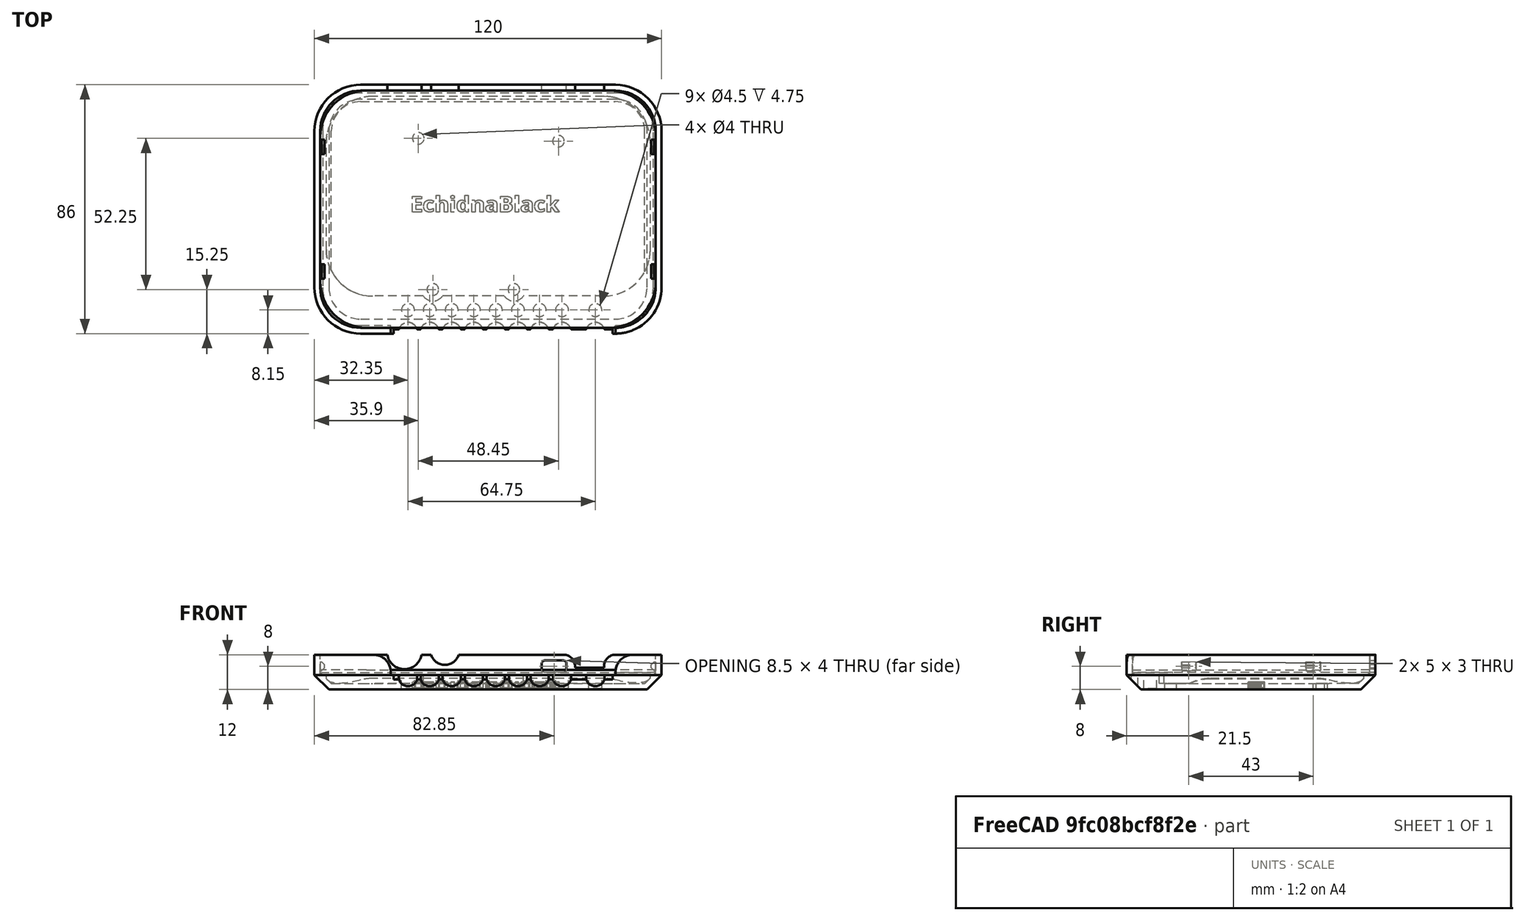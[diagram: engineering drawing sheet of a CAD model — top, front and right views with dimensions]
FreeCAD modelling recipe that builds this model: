
FCSTD DOCUMENT  (FreeCAD 0.18R4 (GitTag))
Label: Caixa_EchidaBlack_baja
License: All rights reserved
LicenseURL: http://en.wikipedia.org/wiki/All_rights_reserved
objects: Part::Cylinder×29, Part::Box×14, Part::Fillet×11, Part::Cut×11, Part::MultiFuse×8, Part::Chamfer×6, Part::Thickness×2, Part::Part2DObjectPython×1, Part::Extrusion×1, Mesh::Feature×1
note: 83 computed .brp shape members not serialized (recipe doc carries the construction recipe); baked Part::Feature solids carry a one-line shape summary decoded from their .brp

FEATURE [Part::Box] Box006  label="Cubo006"
  AttacherType = Attacher::AttachEngine3D
  Height = 9
  Length = 10
  Placement = pos=(83,76,0.5) rot=(0,0,1;0rad)
  Width = 8
FEATURE [Part::Box] Box013  label="Cubo013"
  AttacherType = Attacher::AttachEngine3D
  Height = 12
  Length = 77.75
  Placement = pos=(19.25,-4,-2) rot=(0,0,1;0rad)
  Width = 10
FEATURE [Part::Cylinder] Cylinder005  label="Cilindro005"
  Angle = 360
  AttacherType = Attacher::AttachEngine3D
  Height = 12
  Placement = pos=(32.75,5.15,-9) rot=(0,0,1;0rad)
  Radius = 2.25
FEATURE [Part::Cylinder] Cylinder006  label="Cilindro006"
  Angle = 360
  AttacherType = Attacher::AttachEngine3D
  Height = 12
  Placement = pos=(25.25,5.15,-9) rot=(0,0,1;0rad)
  Radius = 2.25
FEATURE [Part::Cylinder] Cylinder007  label="Cilindro007"
  Angle = 360
  AttacherType = Attacher::AttachEngine3D
  Height = 12
  Placement = pos=(40.35,5.15,-9) rot=(0,0,1;0rad)
  Radius = 2.25
FEATURE [Part::Cylinder] Cylinder008  label="Cilindro008"
  Angle = 360
  AttacherType = Attacher::AttachEngine3D
  Height = 12
  Placement = pos=(48,5.15,-9) rot=(0,0,1;0rad)
  Radius = 2.25
FEATURE [Part::Cylinder] Cylinder009  label="Cilindro009"
  Angle = 360
  AttacherType = Attacher::AttachEngine3D
  Height = 12
  Placement = pos=(55.6,5.15,-9) rot=(0,0,1;0rad)
  Radius = 2.25
FEATURE [Part::Cylinder] Cylinder010  label="Cilindro010"
  Angle = 360
  AttacherType = Attacher::AttachEngine3D
  Height = 12
  Placement = pos=(63.25,5.15,-9) rot=(0,0,1;0rad)
  Radius = 2.25
FEATURE [Part::Cylinder] Cylinder011  label="Cilindro011"
  Angle = 360
  AttacherType = Attacher::AttachEngine3D
  Height = 12
  Placement = pos=(70.75,5.15,-9) rot=(0,0,1;0rad)
  Radius = 2.25
FEATURE [Part::Cylinder] Cylinder012  label="Cilindro012"
  Angle = 360
  AttacherType = Attacher::AttachEngine3D
  Height = 12
  Placement = pos=(70.75,5.15,-9) rot=(0,0,1;0rad)
  Radius = 2.25
FEATURE [Part::Cylinder] Cylinder013  label="Cilindro013"
  Angle = 360
  AttacherType = Attacher::AttachEngine3D
  Height = 12
  Placement = pos=(78.5,5.15,-9) rot=(0,0,1;0rad)
  Radius = 2.25
FEATURE [Part::Cylinder] Cylinder014  label="Cilindro014"
  Angle = 360
  AttacherType = Attacher::AttachEngine3D
  Height = 12
  Placement = pos=(90,5.15,-9) rot=(0,0,1;0rad)
  Radius = 2.25
FEATURE [Part::MultiFuse] Fusion  label="FusionCilindros"
  Placement = pos=(0,0,2.25) rot=(0,0,1;0rad)
  Shapes = -> [Cylinder005,Cylinder006,Cylinder009,Cylinder013,Cylinder011,Cylinder012,Cylinder007,Cylinder008,Cylinder010,Cylinder014]
FEATURE [Part::Part2DObjectPython] ShapeString  # Draft 2D object (typed FeaturePython)
  FontFile = <path>
  MapMode = 5
  Placement = pos=(26,39,-11) rot=(0,0,1;0rad)
  Size = 7
  String = EchidnaBlack
  Tracking = 0
FEATURE [Part::Box] Box016  label="Cubo016"
  AttacherType = Attacher::AttachEngine3D
  Height = 4
  Length = 8.5
  Placement = pos=(72,75,-1) rot=(0,0,1;0rad)
  Width = 8
FEATURE [Part::Cylinder] Cylinder  label="Cilindro"
  Angle = 360
  AttacherType = Attacher::AttachEngine3D
  Height = 10
  Placement = pos=(38,88,6.5) rot=(1,0,0;1.5708rad)
  Radius = 5
FEATURE [Part::Cylinder] Cylinder025  label="Cilindro025"
  Angle = 360
  AttacherType = Attacher::AttachEngine3D
  Height = 10
  Placement = pos=(24,88,6) rot=(1,0,0;1.5708rad)
  Radius = 6
FEATURE [Part::Box] Box  label="Cubo"
  AttacherType = Attacher::AttachEngine3D
  Height = 3
  Length = 2
  Placement = pos=(-5.25,27,-2) rot=(0,0,1;0rad)
  Width = 5
FEATURE [Part::Box] Box017  label="Cubo017"
  AttacherType = Attacher::AttachEngine3D
  Height = 3
  Length = 2
  Placement = pos=(109,27,-2) rot=(0,0,1;0rad)
  Width = 5
FEATURE [Part::Chamfer] Chamfer001
  Base = -> Box017
  Edges = 2 edges r=1: [Edge2,Edge4]
  Placement = pos=(0.3,-11,1.5) rot=(0,0,1;0rad)
FEATURE [Part::Box] Box018  label="Cubo018"
  AttacherType = Attacher::AttachEngine3D
  Height = 3
  Length = 2
  Placement = pos=(-5.25,27,-2) rot=(0,0,1;0rad)
  Width = 5
FEATURE [Part::Chamfer] Chamfer002
  Base = -> Box018
  Edges = 2 edges r=1: [Edge6,Edge8]
  Placement = pos=(-0.3,32,1.5) rot=(0,0,1;0rad)
FEATURE [Part::Box] Box019  label="Cubo019"
  AttacherType = Attacher::AttachEngine3D
  Height = 3
  Length = 2
  Placement = pos=(109,27,-2) rot=(0,0,1;0rad)
  Width = 5
FEATURE [Part::Chamfer] Chamfer003
  Base = -> Box019
  Edges = 2 edges r=1: [Edge2,Edge4]
  Placement = pos=(0.3,32,1.5) rot=(0,0,1;0rad)
FEATURE [Part::Fillet] Fillet028
  Base = -> Box016
  Edges = 4 edges r=1: [Edge2,Edge4,Edge6,Edge8]
  Placement = pos=(-0.5,1,0) rot=(0,0,1;0rad)
FEATURE [Part::Cylinder] Cylinder036  label="Cilindro036"
  Angle = 360
  AttacherType = Attacher::AttachEngine3D
  Height = 12
  Placement = pos=(70.75,5.15,-9) rot=(0,0,1;0rad)
  Radius = 3.25
FEATURE [Part::Cylinder] Cylinder037  label="Cilindro037"
  Angle = 360
  AttacherType = Attacher::AttachEngine3D
  Height = 12
  Placement = pos=(70.75,5.15,-9) rot=(0,0,1;0rad)
  Radius = 3.25
FEATURE [Part::Cylinder] Cylinder038  label="Cilindro038"
  Angle = 360
  AttacherType = Attacher::AttachEngine3D
  Height = 12
  Placement = pos=(78.5,5.15,-9) rot=(0,0,1;0rad)
  Radius = 3.25
FEATURE [Part::Cylinder] Cylinder039  label="Cilindro039"
  Angle = 360
  AttacherType = Attacher::AttachEngine3D
  Height = 12
  Placement = pos=(90,5.15,-9) rot=(0,0,1;0rad)
  Radius = 3.25
FEATURE [Part::Cylinder] Cylinder040  label="Cilindro040"
  Angle = 360
  AttacherType = Attacher::AttachEngine3D
  Height = 12
  Placement = pos=(32.75,5.15,-9) rot=(0,0,1;0rad)
  Radius = 3.25
FEATURE [Part::Cylinder] Cylinder041  label="Cilindro041"
  Angle = 360
  AttacherType = Attacher::AttachEngine3D
  Height = 12
  Placement = pos=(25.25,5.15,-9) rot=(0,0,1;0rad)
  Radius = 3.25
FEATURE [Part::Cylinder] Cylinder042  label="Cilindro042"
  Angle = 360
  AttacherType = Attacher::AttachEngine3D
  Height = 12
  Placement = pos=(40.35,5.15,-9) rot=(0,0,1;0rad)
  Radius = 3.25
FEATURE [Part::Cylinder] Cylinder043  label="Cilindro043"
  Angle = 360
  AttacherType = Attacher::AttachEngine3D
  Height = 12
  Placement = pos=(48,5.15,-9) rot=(0,0,1;0rad)
  Radius = 3.25
FEATURE [Part::Cylinder] Cylinder044  label="Cilindro044"
  Angle = 360
  AttacherType = Attacher::AttachEngine3D
  Height = 12
  Placement = pos=(55.6,5.15,-9) rot=(0,0,1;0rad)
  Radius = 3.25
FEATURE [Part::Cylinder] Cylinder045  label="Cilindro045"
  Angle = 360
  AttacherType = Attacher::AttachEngine3D
  Height = 12
  Placement = pos=(63.25,5.15,-9) rot=(0,0,1;0rad)
  Radius = 3.25
FEATURE [Part::MultiFuse] Fusion003  label="FusionCilindros002"
  Placement = pos=(0,-7.5,1) rot=(0,0,1;0rad)
  Shapes = -> [Cylinder040,Cylinder041,Cylinder044,Cylinder038,Cylinder036,Cylinder037,Cylinder042,Cylinder043,Cylinder045,Cylinder039]
FEATURE [Part::Cylinder] Cylinder046  label="Cilindro046"
  Angle = 120
  AttacherType = Attacher::AttachEngine3D
  Height = 76
  Placement = pos=(20,-2,-2) rot=(0,1,0;1.5708rad)
  Radius = 4
FEATURE [Part::Thickness] Thickness002
  Faces = -> Cylinder046 [Face4,Face5]
  Intersection = false
  Join = 0
  Mode = 0
  Placement = pos=(0,0,6) rot=(0,0,1;3.14159rad)
  SelfIntersection = false
  Value = 2
FEATURE [Part::Box] Box021  label="Cubo021"
  AttacherType = Attacher::AttachEngine3D
  Height = 25
  Length = 5
  Placement = pos=(-20.255,-11,-9) rot=(0,0,1;0rad)
  Width = 17
FEATURE [Part::Box] Box022  label="Cubo022"
  AttacherType = Attacher::AttachEngine3D
  Height = 25
  Length = 5
  Placement = pos=(-101,-11,-9) rot=(0,0,1;0rad)
  Width = 17
FEATURE [Part::Cut] Cut013
  Base = -> Thickness002
  Tool = -> Box021
FEATURE [Part::Cut] Cut014  label="Cilindro_chaflan"
  Base = -> Cut013
  Placement = pos=(0,0.5,1) rot=(0,1,0;3.14159rad)
  Tool = -> Box022
FEATURE [Part::Chamfer] Chamfer
  Base = -> Box
  Edges = 2 edges r=1: [Edge6,Edge8]
  Placement = pos=(-0.3,-11,1.5) rot=(0,0,1;0rad)
FEATURE [Part::Extrusion] Extrude  label="Texto"
  Base = -> ShapeString
  Dir = (0,0,1)
  DirMode = 2
  FaceMakerClass = Part::FaceMakerBullseye
  LengthFwd = 2
  LengthRev = 0
  Placement = pos=(0,0,4.5) rot=(0,0,1;0rad)
  Solid = false
  Symmetric = false
FEATURE [Part::MultiFuse] Fusion006  label="aletas"
  Shapes = -> [Chamfer,Chamfer002,Chamfer001,Chamfer003]
FEATURE [Part::Box] Box020  label="Cubo020"
  AttacherType = Attacher::AttachEngine3D
  Height = 1.7
  Length = 116
  Placement = pos=(-5.1,-1,-12) rot=(0,0,1;0rad)
  Width = 82
FEATURE [Mesh::Feature] EchidnaBlack_0
  Placement = pos=(-0.35,-0.085,-1) rot=(0,0,1;0rad)
FEATURE [Part::Fillet] Fillet
  Base = -> Box020
  Edges = 1 edges r=16: [Edge7]
FEATURE [Part::Fillet] Fillet029
  Base = -> Fillet
  Edges = 3 edges r=16: [Edge3,Edge12,Edge15]
  Placement = pos=(0,0,10) rot=(0,0,1;0rad)
FEATURE [Part::Box] Box023  label="Cubo023"
  AttacherType = Attacher::AttachEngine3D
  Height = 12
  Length = 120
  Placement = pos=(-7.1,-3,-20) rot=(0,0,1;0rad)
  Width = 86
FEATURE [Part::Fillet] Fillet030
  Base = -> Box023
  Edges = 1 edges r=16: [Edge7]
FEATURE [Part::Fillet] Fillet031
  Base = -> Fillet030
  Edges = 3 edges r=16: [Edge3,Edge12,Edge15]
  Placement = pos=(0,0,13) rot=(0,0,1;0rad)
FEATURE [Part::Chamfer] Chamfer004
  Base = -> Fillet031
  Edges = 7 edges r=5: [Edge4,Edge12,Edge14,Edge16,Edge17,Edge18,Edge19]
FEATURE [Part::Thickness] Thickness
  Faces = -> Chamfer004 [Face4]
  Intersection = false
  Join = 0
  Mode = 0
  SelfIntersection = false
  Value = -2
FEATURE [Part::Box] Box025  label="Cubo025"
  AttacherType = Attacher::AttachEngine3D
  Height = 8
  Length = 112
  Placement = pos=(-3,10,-21) rot=(0,0,1;0rad)
  Width = 69
FEATURE [Part::Fillet] Fillet035
  Base = -> Box025
  Edges = 1 edges r=16: [Edge7]
FEATURE [Part::Fillet] Fillet034
  Base = -> Fillet035
  Edges = 3 edges r=16: [Edge3,Edge12,Edge15]
  Placement = pos=(0,0,13) rot=(0,0,1;0rad)
FEATURE [Part::Cut] Cut
  Base = -> Thickness
  Tool = -> Box013
FEATURE [Part::Box] Box026  label="Cubo026"
  AttacherType = Attacher::AttachEngine3D
  Height = 6
  Length = 120
  Placement = pos=(-7.1,-3,-20) rot=(0,0,1;0rad)
  Width = 86
FEATURE [Part::Fillet] Fillet036
  Base = -> Box026
  Edges = 1 edges r=16: [Edge7]
FEATURE [Part::Fillet] Fillet037
  Base = -> Fillet036
  Edges = 3 edges r=16: [Edge3,Edge12,Edge15]
  Placement = pos=(0,0,13) rot=(0,0,1;0rad)
FEATURE [Part::Chamfer] Chamfer005
  Base = -> Fillet037
  Edges = 7 edges r=5: [Edge4,Edge12,Edge14,Edge16,Edge17,Edge18,Edge19]
FEATURE [Part::Box] Box027  label="Cubo027"
  AttacherType = Attacher::AttachEngine3D
  Height = 12
  Length = 121.75
  Placement = pos=(-7.75,-4,-2) rot=(0,0,1;0rad)
  Width = 89
FEATURE [Part::Cut] Cut023
  Base = -> Chamfer005
  Tool = -> Box027
FEATURE [Part::Cut] Cut024
  Base = -> Cut023
  Tool = -> Fillet034
FEATURE [Part::MultiFuse] Fusion007
  Shapes = -> [Cut,Cut024]
FEATURE [Part::Cut] Cut025
  Base = -> Fusion007
  Tool = -> Fusion
FEATURE [Part::Cut] Cut026
  Base = -> Cut025
  Tool = -> Fusion003
FEATURE [Part::Cut] Cut027
  Base = -> Cut026
  Tool = -> Cut014
FEATURE [Part::Fillet] Fillet038
  Base = -> Cut027
  Edges = 2 edges r=6: [Edge16,Edge25]
FEATURE [Part::MultiFuse] Fusion008
  Shapes = -> [Cylinder,Cylinder025,Fillet028,Box006]
FEATURE [Part::Cut] Cut028
  Base = -> Fillet038
  Tool = -> Fusion008
FEATURE [Part::Fillet] Fillet039
  Base = -> Cut028
  Edges = 2 edges r=4: [Edge11,Edge121]
FEATURE [Part::Cylinder] Cylinder047  label="Cilindro047"
  Angle = 360
  AttacherType = Attacher::AttachEngine3D
  Height = 10
  Placement = pos=(33.85,12.25,-14) rot=(0,0,1;0rad)
  Radius = 2
FEATURE [Part::Cylinder] Cylinder048  label="Cilindro048"
  Angle = 360
  AttacherType = Attacher::AttachEngine3D
  Height = 10
  Placement = pos=(28.8,64.5,-14) rot=(0,0,1;0rad)
  Radius = 2
FEATURE [Part::Cylinder] Cylinder049  label="Cilindro049"
  Angle = 360
  AttacherType = Attacher::AttachEngine3D
  Height = 10
  Placement = pos=(61.85,12.25,-14) rot=(0,0,1;0rad)
  Radius = 2
FEATURE [Part::Cylinder] Cylinder050  label="Cilindro050"
  Angle = 360
  AttacherType = Attacher::AttachEngine3D
  Height = 10
  Placement = pos=(77.25,63.5,-14) rot=(0,0,1;0rad)
  Radius = 2
FEATURE [Part::MultiFuse] Fusion009
  Shapes = -> [Cylinder047,Cylinder048,Cylinder049,Cylinder050]
FEATURE [Part::Cylinder] Cylinder051  label="Cilindro051"
  Angle = 360
  AttacherType = Attacher::AttachEngine3D
  Height = 10
  Placement = pos=(33.85,12.25,-5) rot=(0,0,1;0rad)
  Radius = 4
FEATURE [Part::Cylinder] Cylinder053  label="Cilindro053"
  Angle = 360
  AttacherType = Attacher::AttachEngine3D
  Height = 10
  Placement = pos=(61.85,12.25,-5) rot=(0,0,1;0rad)
  Radius = 4
FEATURE [Part::Cut] Cut029
  Base = -> Fillet039
  Tool = -> Fusion009
FEATURE [Part::MultiFuse] Fusion010
  Shapes = -> [Cylinder051,Cylinder053]
FEATURE [Part::Cut] Cut030
  Base = -> Cut029
  Tool = -> Fusion010
FEATURE [Part::MultiFuse] Fusion011
  Shapes = -> [Fusion006,Cut030]
note: 1 file-system path scrubbed to <path> (originals preserved in the JSON sidecar)
